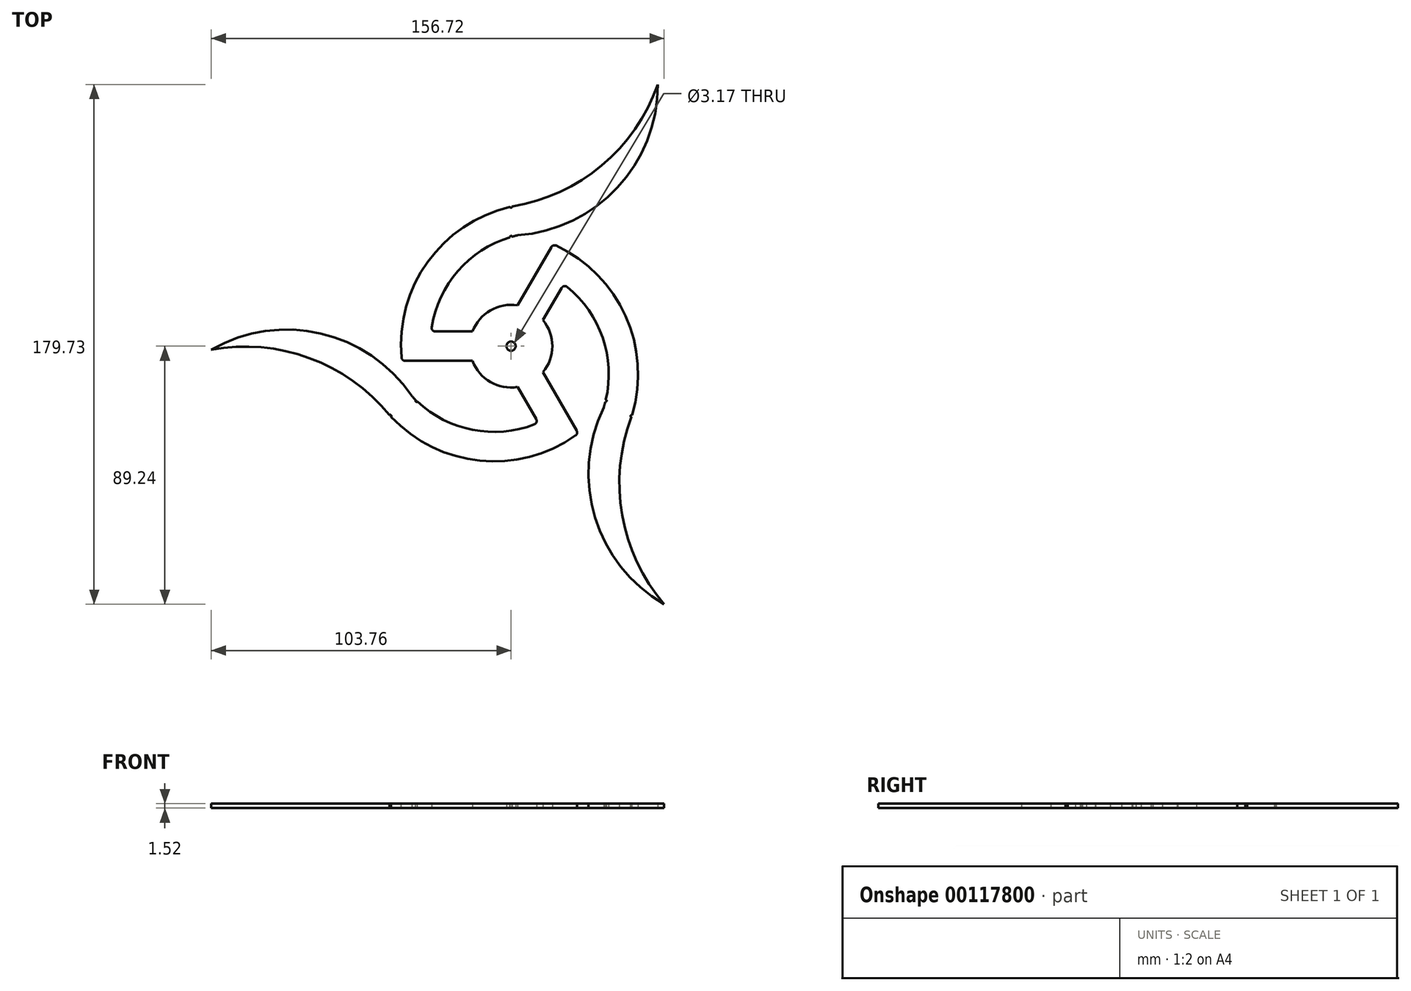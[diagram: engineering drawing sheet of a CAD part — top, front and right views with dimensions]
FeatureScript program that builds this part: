
annotation { "Feature Type Name" : "Feature", "Feature Type Description" : "" }
export const myFeature = defineFeature(function(context is Context, id is Id, definition is map)
    precondition{}
    {
        {
            var Q0;
            Q0=qCreatedBy(makeId("Top.planeOp"),FACE);
            var sketch = newSketch(context, id + "F0", { "sketchPlane" : qUnion([Q0])});
            skCircle(sketch, "E0", {"center": v(0, 0) * mm, "radius": 90.49 * mm, "construction": true});
            skCircle(sketch, "E1", {"center": v(0, 0) * mm, "radius": 14.29 * mm});
            skCircle(sketch, "E2", {"center": v(0, 0) * mm, "radius": 1.59 * mm});
            skLineSegment(sketch, "E3", {"start": v(0, 0) * mm, "end": v(-38.1, 0) * mm, "construction": true});
            skCircle(sketch, "E4", {"center": v(0, 0) * mm, "radius": 48.26 * mm, "construction": true});
            skLineSegment(sketch, "E5", {"start": v(0, 90.49) * mm, "end": v(50.8, 90.49) * mm, "construction": true});
            skLineSegment(sketch, "E6", {"start": v(50.8, 90.49) * mm, "end": v(50.8, 67.63) * mm, "construction": true});
            skLineSegment(sketch, "E7", {"start": v(50.8, 67.63) * mm, "end": v(36.83, 67.63) * mm, "construction": true});
            skLineSegment(sketch, "E8", {"start": v(0, 90.49) * mm, "end": v(0, 48.26) * mm, "construction": true});
            skArc(sketch, "E9", {"start": v(0, 48.26) * mm, "mid": v(-27.56, 30.85) * mm, "end": v(-38.1, 0) * mm});
            skArc(sketch, "E10", {"start": v(0, 48.26) * mm, "mid": v(31.22, 62.37) * mm, "end": v(50.8, 90.49) * mm});
            skArc(sketch, "E11.0", {"start": v(2.26, 38.36) * mm, "mid": v(-19.58, 24.55) * mm, "end": v(-27.94, 0.1) * mm});
            skArc(sketch, "E12", {"start": v(2.26, 38.36) * mm, "mid": v(36.79, 54.87) * mm, "end": v(50.8, 90.49) * mm});
            skLineSegment(sketch, "E13", {"start": v(-27.94, 0.1) * mm, "end": v(-38.1, 0) * mm});
            skLineSegment(sketch, "E14", {"start": v(0, 0) * mm, "end": v(0, 48.26) * mm, "construction": true});
            skSolve(sketch);
        }
        {
            var Q0;
            Q0=makeQuery(id+"F0.imprint","IMPRINT",FACE,{"disambiguationData":[TD([[makeQuery(id+"F0.imprint","IMPRINT",EDGE,{"derivedFrom":sQuery(id+"F0.wireOp",EDGE,"E9")}),1.0]])]});
            var sketch = newSketch(context, id + "F1", { "sketchPlane" : qUnion([Q0])});
            skCircle(sketch, "E15.0", {"center": v(0, 0) * mm, "radius": 14.29 * mm});
            skArc(sketch, "E16.0", {"start": v(2.26, 38.36) * mm, "mid": v(-17.47, 27) * mm, "end": v(-27.46, 6.55) * mm});
            skLineSegment(sketch, "E17", {"start": v(-13.35, 5.08) * mm, "end": v(-26.2, 5.08) * mm});
            skPoint(sketch, "E18.orphan", {"position": v(-38.1, 0) * mm});
            skArc(sketch, "E19.0", {"start": v(0, 48.26) * mm, "mid": v(-28.74, 29.28) * mm, "end": v(-37.9, -3.92) * mm});
            skLineSegment(sketch, "E20", {"start": v(-13.35, -5.08) * mm, "end": v(-36.64, -5.08) * mm});
            skPoint(sketch, "E21.visualSharp", {"position": v(-37.79, -5.08) * mm});
            skArc(sketch, "E21.filletArc", {"start": v(-37.9, -3.92) * mm, "mid": v(-37.5, -4.75) * mm, "end": v(-36.64, -5.08) * mm});
            skPoint(sketch, "E22.newPointA", {"position": v(-27.94, 0.1) * mm});
            skArc(sketch, "E22.filletArc", {"start": v(-27.46, 6.55) * mm, "mid": v(-27.18, 5.53) * mm, "end": v(-26.2, 5.08) * mm});
            skSolve(sketch);
        }
        {
            var Q0;
            Q0=makeQuery(id+"F0.imprint","IMPRINT",FACE,{"disambiguationData":[TD([[makeQuery(id+"F0.imprint","IMPRINT",EDGE,{"derivedFrom":sQuery(id+"F0.wireOp",EDGE,"E9")}),1.0]])]});
            var Q1;
            {var subQ3=sQuery(id+"F1.wireOp",EDGE,"E17");Q1=makeQuery(id+"F1.imprint","IMPRINT",FACE,{"disambiguationData":[TD([[makeQuery(id+"F1.imprint","IMPRINT",EDGE,{"derivedFrom":subQ3}),1.0]])]});}
            var Q2;
            Q2=makeQuery(id+"F0.imprint","IMPRINT",FACE,{"disambiguationData":[TD([[makeQuery(id+"F0.imprint","IMPRINT",EDGE,{"derivedFrom":sQuery(id+"F0.wireOp",EDGE,"E1")}),1.0]])]});
            extrude(context, id + "F2", {"entities" : qUnion([Q0, Q1, Q2]), "depth" : 1.52 * mm});
        }
        {
            var Q0;
            Q0=makeQuery(id+"F2.opExtrude","SWEPT_BODY",BODY,{"disambiguationData":[OSD([sQuery(id+"F0.wireOp",EDGE,"E9"),sQuery(id+"F0.wireOp",EDGE,"E10"),sQuery(id+"F0.wireOp",EDGE,"E11.0"),sQuery(id+"F0.wireOp",EDGE,"E12"),sQuery(id+"F0.wireOp",EDGE,"E13")])]});
            var Q1;
            Q1=makeQuery(id+"F2.opExtrude","SWEPT_BODY",BODY,{"disambiguationData":[OSD([sQuery(id+"F0.wireOp",EDGE,"E13"),sQuery(id+"F1.wireOp",EDGE,"E15.0"),sQuery(id+"F1.wireOp",EDGE,"E16.0"),sQuery(id+"F1.wireOp",EDGE,"E17"),sQuery(id+"F1.wireOp",EDGE,"E19.0"),sQuery(id+"F1.wireOp",EDGE,"E20")])]});
            var Q2;
            Q2=makeQuery(id+"F2.opExtrude","CAP_EDGE",EDGE,{"disambiguationData":[OSD([sQuery(id+"F0.wireOp",EDGE,"E2")])],"isStart":true});
            circularPattern(context, id + "F3", {"entities" : qUnion([Q0, Q1]), "axis" : qUnion([Q2]), "angle" : 120 * degree, "instanceCount" : 3});
        }
        {
            var Q0;
            Q0=makeQuery(id+"F2.opExtrude","SWEPT_BODY",BODY,{"disambiguationData":[OSD([sQuery(id+"F0.wireOp",EDGE,"E9"),sQuery(id+"F0.wireOp",EDGE,"E10"),sQuery(id+"F0.wireOp",EDGE,"E11.0"),sQuery(id+"F0.wireOp",EDGE,"E12"),sQuery(id+"F0.wireOp",EDGE,"E13")])]});
            var Q1;
            Q1=makeQuery(id+"F2.opExtrude","SWEPT_BODY",BODY,{"disambiguationData":[OSD([sQuery(id+"F0.wireOp",EDGE,"E13"),sQuery(id+"F1.wireOp",EDGE,"E15.0"),sQuery(id+"F1.wireOp",EDGE,"E16.0"),sQuery(id+"F1.wireOp",EDGE,"E17"),sQuery(id+"F1.wireOp",EDGE,"E19.0"),sQuery(id+"F1.wireOp",EDGE,"E20")])]});
            var Q2;
            Q2=makeQuery(id+"F2.opExtrude","SWEPT_BODY",BODY,{"disambiguationData":[OSD([sQuery(id+"F0.wireOp",EDGE,"E1"),sQuery(id+"F0.wireOp",EDGE,"E2")])]});
            var Q3;
            Q3=makeQuery(id+"F3.opPattern","COPY",BODY,{"derivedFrom":makeQuery(id+"F2.opExtrude","SWEPT_BODY",BODY,{"disambiguationData":[OSD([sQuery(id+"F0.wireOp",EDGE,"E13"),sQuery(id+"F1.wireOp",EDGE,"E15.0"),sQuery(id+"F1.wireOp",EDGE,"E16.0"),sQuery(id+"F1.wireOp",EDGE,"E17"),sQuery(id+"F1.wireOp",EDGE,"E19.0"),sQuery(id+"F1.wireOp",EDGE,"E20")])]}),"instanceName":"2"});
            var Q4;
            Q4=makeQuery(id+"F3.opPattern","COPY",BODY,{"derivedFrom":makeQuery(id+"F2.opExtrude","SWEPT_BODY",BODY,{"disambiguationData":[OSD([sQuery(id+"F0.wireOp",EDGE,"E9"),sQuery(id+"F0.wireOp",EDGE,"E10"),sQuery(id+"F0.wireOp",EDGE,"E11.0"),sQuery(id+"F0.wireOp",EDGE,"E12"),sQuery(id+"F0.wireOp",EDGE,"E13")])]}),"instanceName":"2"});
            var Q5;
            Q5=makeQuery(id+"F3.opPattern","COPY",BODY,{"derivedFrom":makeQuery(id+"F2.opExtrude","SWEPT_BODY",BODY,{"disambiguationData":[OSD([sQuery(id+"F0.wireOp",EDGE,"E13"),sQuery(id+"F1.wireOp",EDGE,"E15.0"),sQuery(id+"F1.wireOp",EDGE,"E16.0"),sQuery(id+"F1.wireOp",EDGE,"E17"),sQuery(id+"F1.wireOp",EDGE,"E19.0"),sQuery(id+"F1.wireOp",EDGE,"E20")])]}),"instanceName":"1"});
            var Q6;
            Q6=makeQuery(id+"F3.opPattern","COPY",BODY,{"derivedFrom":makeQuery(id+"F2.opExtrude","SWEPT_BODY",BODY,{"disambiguationData":[OSD([sQuery(id+"F0.wireOp",EDGE,"E9"),sQuery(id+"F0.wireOp",EDGE,"E10"),sQuery(id+"F0.wireOp",EDGE,"E11.0"),sQuery(id+"F0.wireOp",EDGE,"E12"),sQuery(id+"F0.wireOp",EDGE,"E13")])]}),"instanceName":"1"});
            booleanBodies(context, id + "F4", {"operationType" : BooleanOperationType.UNION, "tools" : qUnion([Q0, Q1, Q2, Q3, Q4, Q5, Q6])});
        }
        {
            var Q0;
            {var subQ0=sQuery(id+"F0.wireOp",EDGE,"E13");var subQ1=sQuery(id+"F0.wireOp",EDGE,"E11.0");var subQ2=makeQuery(id+"F2.opExtrude","CAP_FACE",FACE,{"disambiguationData":[OSD([subQ1,subQ0,sQuery(id+"F1.wireOp",EDGE,"E15.0"),sQuery(id+"F1.wireOp",EDGE,"E17"),sQuery(id+"F1.wireOp",EDGE,"E19.0"),sQuery(id+"F1.wireOp",EDGE,"E20"),sQuery(id+"F1.wireOp",EDGE,"E21.filletArc"),sQuery(id+"F1.wireOp",EDGE,"E22.filletArc")])],"isStart":false});var subQ3=makeQuery(id+"F2.opExtrude","CAP_FACE",FACE,{"disambiguationData":[OSD([sQuery(id+"F0.wireOp",EDGE,"E9"),sQuery(id+"F0.wireOp",EDGE,"E10"),subQ1,sQuery(id+"F0.wireOp",EDGE,"E12"),subQ0])],"isStart":false});Q0=makeQuery(id+"F4.opBoolean","MERGE",FACE,{"derivedFrom":[makeQuery(id+"F2.opExtrude","CAP_FACE",FACE,{"disambiguationData":[OSD([sQuery(id+"F0.wireOp",EDGE,"E1"),sQuery(id+"F0.wireOp",EDGE,"E2")])],"isStart":false}),subQ3,subQ2,makeQuery(id+"F3.opPattern","COPY",FACE,{"derivedFrom":subQ3,"instanceName":"1"}),makeQuery(id+"F3.opPattern","COPY",FACE,{"derivedFrom":subQ2,"instanceName":"1"}),makeQuery(id+"F3.opPattern","COPY",FACE,{"derivedFrom":subQ3,"instanceName":"2"}),makeQuery(id+"F3.opPattern","COPY",FACE,{"derivedFrom":subQ2,"instanceName":"2"})]});}
            var sketch = newSketch(context, id + "F5", { "sketchPlane" : qUnion([Q0])});
            skPoint(sketch, "E23.0", {"position": v(0, 0) * mm});
            skLineSegment(sketch, "E24", {"start": v(0, 0) * mm, "end": v(0, 52.15) * mm, "construction": true});
            skCircle(sketch, "E25", {"center": v(0, 48.26) * mm, "radius": 0.38 * mm});
            skCircle(sketch, "E26", {"center": v(0, 37.77) * mm, "radius": 0.38 * mm});
            skCircle(sketch, "E27.1.0", {"center": v(-41.8, -24.13) * mm, "radius": 0.38 * mm});
            skCircle(sketch, "E27.1.1", {"center": v(-32.7, -18.88) * mm, "radius": 0.38 * mm});
            skCircle(sketch, "E27.2.0", {"center": v(41.8, -24.13) * mm, "radius": 0.38 * mm});
            skCircle(sketch, "E27.2.1", {"center": v(32.7, -18.88) * mm, "radius": 0.38 * mm});
            skSolve(sketch);
        }
        {
            var Q0;
            {var subQ0=sQuery(id+"F5.wireOp",EDGE,"E25");var subQ1=makeQuery(id+"F2.opExtrude","CAP_EDGE",EDGE,{"disambiguationData":[OSD([sQuery(id+"F0.wireOp",EDGE,"E10")])],"isStart":false});var subQ2=makeQuery(id+"F5.imprint","INTERSECT",VERTEX,{"derivedFrom":[subQ1,subQ0]});Q0=makeQuery(id+"F5.imprint","IMPRINT",FACE,{"disambiguationData":[TD([[makeQuery(id+"F5.imprint","IMPRINT",EDGE,{"disambiguationData":[TD([[subQ2,-1.0]])],"derivedFrom":subQ0}),1.0]])]});}
            var Q1;
            {var subQ0=sQuery(id+"F5.wireOp",EDGE,"E25");var subQ1=makeQuery(id+"F2.opExtrude","CAP_EDGE",EDGE,{"disambiguationData":[OSD([sQuery(id+"F0.wireOp",EDGE,"E10")])],"isStart":false});var subQ2=makeQuery(id+"F5.imprint","INTERSECT",VERTEX,{"derivedFrom":[subQ1,subQ0]});Q1=makeQuery(id+"F5.imprint","IMPRINT",FACE,{"disambiguationData":[TD([[makeQuery(id+"F5.imprint","IMPRINT",EDGE,{"disambiguationData":[TD([[subQ2,1.0]])],"derivedFrom":subQ0}),1.0]])]});}
            var Q2;
            {var subQ0=sQuery(id+"F5.wireOp",EDGE,"E26");var subQ1=sQuery(id+"F0.wireOp",EDGE,"E11.0");var subQ2=makeQuery(id+"F2.opExtrude","CAP_EDGE",EDGE,{"disambiguationData":[OSD([subQ1]),TDD([makeQuery(id+"F0.imprint","IMPRINT",EDGE,{"derivedFrom":subQ1})])],"isStart":false});var subQ3=makeQuery(id+"F5.imprint","INTERSECT",VERTEX,{"disambiguationData":[OD(0.0)],"derivedFrom":[subQ2,subQ0]});Q2=makeQuery(id+"F5.imprint","IMPRINT",FACE,{"disambiguationData":[TD([[makeQuery(id+"F5.imprint","IMPRINT",EDGE,{"disambiguationData":[TD([[subQ3,-1.0]])],"derivedFrom":subQ0}),1.0]])]});}
            var Q3;
            {var subQ0=sQuery(id+"F5.wireOp",EDGE,"E27.1.0");var subQ1=makeQuery(id+"F3.opPattern","COPY",EDGE,{"derivedFrom":makeQuery(id+"F2.opExtrude","CAP_EDGE",EDGE,{"disambiguationData":[OSD([sQuery(id+"F0.wireOp",EDGE,"E10")])],"isStart":false}),"instanceName":"1"});var subQ2=makeQuery(id+"F5.imprint","INTERSECT",VERTEX,{"derivedFrom":[subQ1,subQ0]});Q3=makeQuery(id+"F5.imprint","IMPRINT",FACE,{"disambiguationData":[TD([[makeQuery(id+"F5.imprint","IMPRINT",EDGE,{"disambiguationData":[TD([[subQ2,1.0]])],"derivedFrom":subQ0}),1.0]])]});}
            var Q4;
            {var subQ0=sQuery(id+"F5.wireOp",EDGE,"E27.1.1");var subQ1=sQuery(id+"F0.wireOp",EDGE,"E11.0");var subQ2=makeQuery(id+"F3.opPattern","COPY",EDGE,{"derivedFrom":makeQuery(id+"F2.opExtrude","CAP_EDGE",EDGE,{"disambiguationData":[OSD([subQ1]),TDD([makeQuery(id+"F0.imprint","IMPRINT",EDGE,{"derivedFrom":subQ1})])],"isStart":false}),"instanceName":"1"});var subQ3=makeQuery(id+"F5.imprint","INTERSECT",VERTEX,{"disambiguationData":[OD(0.0)],"derivedFrom":[subQ2,subQ0]});Q4=makeQuery(id+"F5.imprint","IMPRINT",FACE,{"disambiguationData":[TD([[makeQuery(id+"F5.imprint","IMPRINT",EDGE,{"disambiguationData":[TD([[subQ3,-1.0]])],"derivedFrom":subQ0}),1.0]])]});}
            var Q5;
            {var subQ0=sQuery(id+"F5.wireOp",EDGE,"E27.2.1");var subQ1=sQuery(id+"F0.wireOp",EDGE,"E11.0");var subQ2=makeQuery(id+"F3.opPattern","COPY",EDGE,{"derivedFrom":makeQuery(id+"F2.opExtrude","CAP_EDGE",EDGE,{"disambiguationData":[OSD([subQ1]),TDD([makeQuery(id+"F0.imprint","IMPRINT",EDGE,{"derivedFrom":subQ1})])],"isStart":false}),"instanceName":"2"});var subQ3=makeQuery(id+"F5.imprint","INTERSECT",VERTEX,{"disambiguationData":[OD(0.0)],"derivedFrom":[subQ2,subQ0]});Q5=makeQuery(id+"F5.imprint","IMPRINT",FACE,{"disambiguationData":[TD([[makeQuery(id+"F5.imprint","IMPRINT",EDGE,{"disambiguationData":[TD([[subQ3,-1.0]])],"derivedFrom":subQ0}),1.0]])]});}
            var Q6;
            {var subQ0=sQuery(id+"F5.wireOp",EDGE,"E27.2.0");var subQ1=makeQuery(id+"F3.opPattern","COPY",EDGE,{"derivedFrom":makeQuery(id+"F2.opExtrude","CAP_EDGE",EDGE,{"disambiguationData":[OSD([sQuery(id+"F0.wireOp",EDGE,"E10")])],"isStart":false}),"instanceName":"2"});var subQ2=makeQuery(id+"F5.imprint","INTERSECT",VERTEX,{"derivedFrom":[subQ1,subQ0]});Q6=makeQuery(id+"F5.imprint","IMPRINT",FACE,{"disambiguationData":[TD([[makeQuery(id+"F5.imprint","IMPRINT",EDGE,{"disambiguationData":[TD([[subQ2,1.0]])],"derivedFrom":subQ0}),1.0]])]});}
            extrude(context, id + "F6", {"entities" : qUnion([Q0, Q1, Q2, Q3, Q4, Q5, Q6]), "operationType" : NewBodyOperationType.REMOVE, "endBound" : BoundingType.UP_TO_NEXT, "oppositeDirection" : true, "depth" : 25.4 * mm});
        }
    });
